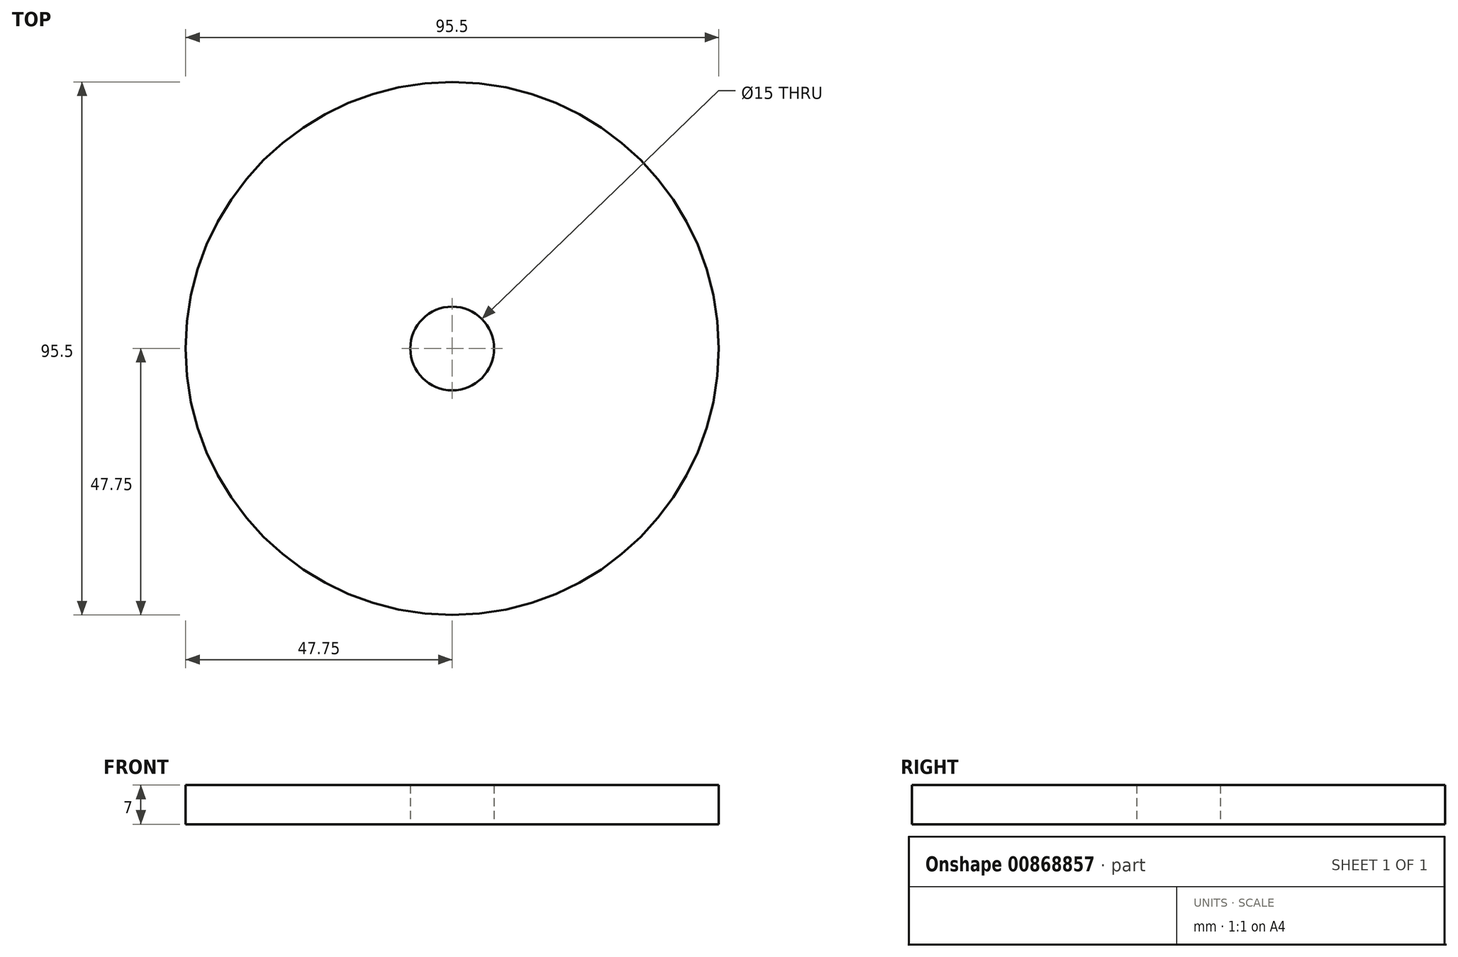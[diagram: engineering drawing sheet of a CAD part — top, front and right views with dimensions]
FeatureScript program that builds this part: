
annotation { "Feature Type Name" : "Feature", "Feature Type Description" : "" }
export const myFeature = defineFeature(function(context is Context, id is Id, definition is map)
    precondition{}
    {
        {
            var Q0;
            Q0=qCreatedBy(makeId("Top.planeOp"),FACE);
            var sketch = newSketch(context, id + "F0", { "sketchPlane" : qUnion([Q0])});
            skCircle(sketch, "E0", {"center": v(0, 0) * mm, "radius": 47.75 * mm});
            skCircle(sketch, "E1", {"center": v(0, 0) * mm, "radius": 7.5 * mm});
            skSolve(sketch);
        }
        {
            var Q0;
            Q0=makeQuery(id+"F0.imprint","IMPRINT",FACE,{"disambiguationData":[TD([[makeQuery(id+"F0.imprint","IMPRINT",EDGE,{"derivedFrom":sQuery(id+"F0.wireOp",EDGE,"E0")}),1.0]])]});
            extrude(context, id + "F1", {"entities" : qUnion([Q0]), "depth" : 7 * mm, "offsetDistance" : 25 * mm});
        }
    });
